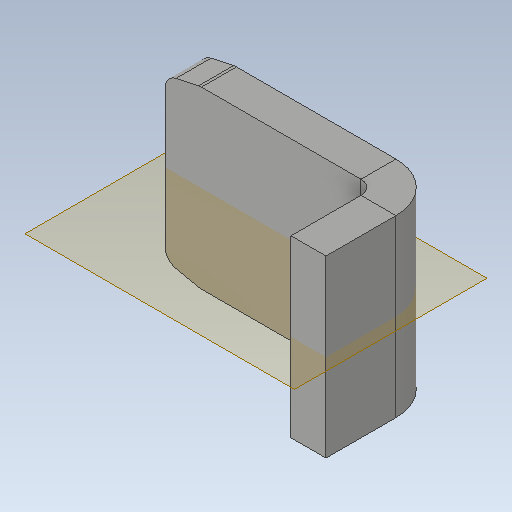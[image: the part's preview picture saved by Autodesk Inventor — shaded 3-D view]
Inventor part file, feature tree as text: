
AUTODESK INVENTOR PART (.ipt)
format: ipt  version: 2020.1 (Build 241239000, 239)  size: 135,168 bytes
history: native  units: mm
features: sheet_metal_op x4, other x3, sketch x2
ambient origin geometry x8: Origin, YZ Plane, XZ Plane, XY Plane, X Axis, Y Axis, Z Axis, Center Point
bodies: Solid1 (feature_tree)
feature tree (9):
  sheet_metal_op  "Face1"
  sheet_metal_op  "Flange1"
  other  "midtplan"
  sketch  "Sketch1"  dims[d2=2.094395mm d3=2.094395mm]
  other  "Plate1"
  sketch  "Sketch2"  dims[d4=25.0mm d5=2.094395mm d7=35.0mm d8=5.0mm d9=5.0mm d10=5.0mm d11=2.5mm d12=10.0mm d13=2.0mm d14=12.0mm d15=90.0deg d16=2.0mm d17=20.0mm d18=5.0mm d19=2.0mm d20=2.0mm]
  other  "Plate2"
  sheet_metal_op  "Bend1"
  sheet_metal_op  "Corner1"
